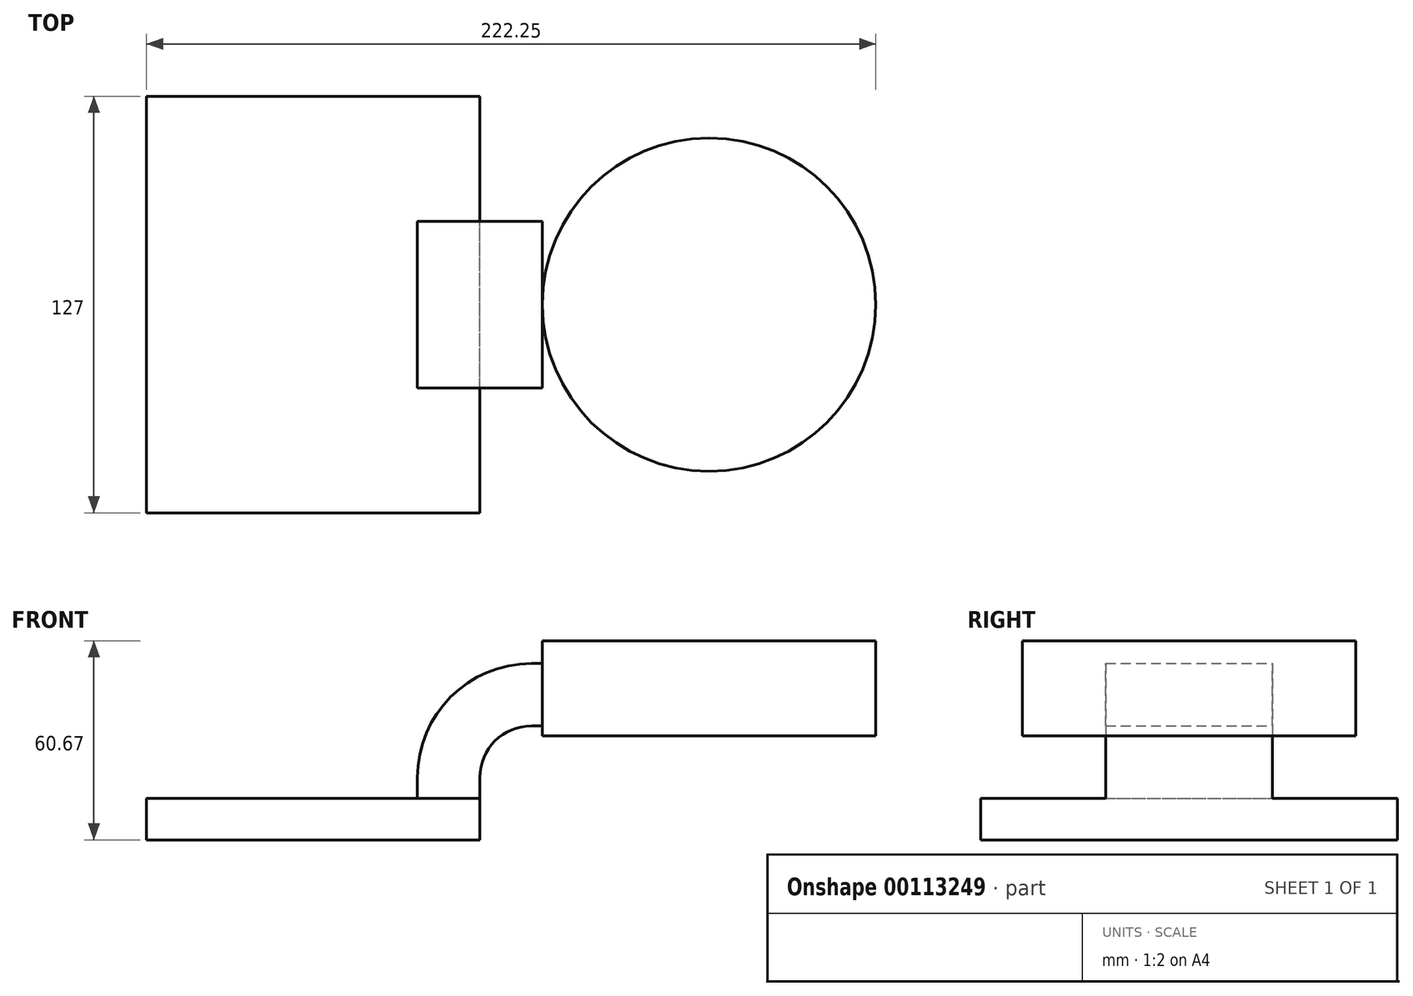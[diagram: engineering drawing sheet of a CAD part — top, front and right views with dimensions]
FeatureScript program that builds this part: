
annotation { "Feature Type Name" : "Feature", "Feature Type Description" : "" }
export const myFeature = defineFeature(function(context is Context, id is Id, definition is map)
    precondition{}
    {
        {
            var Q0;
            Q0=qCreatedBy(makeId("Front.planeOp"),FACE);
            var sketch = newSketch(context, id + "F0", { "sketchPlane" : qUnion([Q0])});
            skLineSegment(sketch, "E0.bottom", {"start": v(50.8, 6.35) * mm, "end": v(-50.8, 6.35) * mm});
            skLineSegment(sketch, "E0.top", {"start": v(50.8, -6.35) * mm, "end": v(-50.8, -6.35) * mm});
            skLineSegment(sketch, "E0.left", {"start": v(50.8, 6.35) * mm, "end": v(50.8, -6.35) * mm});
            skLineSegment(sketch, "E0.right", {"start": v(-50.8, 6.35) * mm, "end": v(-50.8, -6.35) * mm});
            skPoint(sketch, "E0.middle", {"position": v(0, 0) * mm});
            skLineSegment(sketch, "E1.bottom", {"start": v(69.85, 25.4) * mm, "end": v(120.65, 25.4) * mm});
            skLineSegment(sketch, "E1.top", {"start": v(69.85, 54.32) * mm, "end": v(120.65, 54.32) * mm});
            skLineSegment(sketch, "E1.left", {"start": v(69.85, 25.4) * mm, "end": v(69.85, 54.32) * mm});
            skLineSegment(sketch, "E1.right", {"start": v(120.65, 25.4) * mm, "end": v(120.65, 54.32) * mm});
            skPoint(sketch, "E1.middle", {"position": v(95.25, 39.86) * mm});
            skLineSegment(sketch, "E2", {"start": v(50.8, 6.35) * mm, "end": v(50.8, 12.7) * mm});
            skArc(sketch, "E3", {"start": v(50.8, 12.7) * mm, "mid": v(55.39, 23.78) * mm, "end": v(66.47, 28.37) * mm});
            skLineSegment(sketch, "E4", {"start": v(66.47, 28.37) * mm, "end": v(90.85, 28.37) * mm});
            skLineSegment(sketch, "E5.0", {"start": v(66.47, 47.42) * mm, "end": v(90.85, 47.42) * mm});
            skArc(sketch, "E5.1", {"start": v(31.75, 12.7) * mm, "mid": v(41.92, 37.25) * mm, "end": v(66.47, 47.42) * mm});
            skLineSegment(sketch, "E5.2", {"start": v(31.75, 12.7) * mm, "end": v(31.75, 35.55) * mm});
            skLineSegment(sketch, "E6", {"start": v(31.75, 12.7) * mm, "end": v(31.75, 6.35) * mm});
            skSolve(sketch);
        }
        {
            var Q0;
            Q0=makeQuery(id+"F0.imprint","IMPRINT",FACE,{"disambiguationData":[TD([[makeQuery(id+"F0.imprint","IMPRINT",EDGE,{"derivedFrom":sQuery(id+"F0.wireOp",EDGE,"E0.top")}),-1.0]])]});
            extrude(context, id + "F1", {"entities" : qUnion([Q0]), "endBound" : BoundingType.SYMMETRIC, "depth" : 127 * mm});
        }
        {
            var Q0;
            {var subQ2=sQuery(id+"F0.wireOp",EDGE,"E2");Q0=makeQuery(id+"F0.imprint","IMPRINT",FACE,{"disambiguationData":[TD([[makeQuery(id+"F0.imprint","IMPRINT",EDGE,{"derivedFrom":subQ2}),1.0]])]});}
            extrude(context, id + "F2", {"entities" : qUnion([Q0]), "operationType" : NewBodyOperationType.ADD, "endBound" : BoundingType.SYMMETRIC, "depth" : 50.8 * mm});
        }
        {
            var Q0;
            {var subQ3=sQuery(id+"F0.wireOp",EDGE,"E1.bottom");Q0=makeQuery(id+"F0.imprint","IMPRINT",FACE,{"disambiguationData":[TD([[makeQuery(id+"F0.imprint","IMPRINT",EDGE,{"derivedFrom":subQ3}),1.0]])]});}
            var Q1;
            Q1=sQuery(id+"F0.wireOp",EDGE,"E1.right");
            revolve(context, id + "F3", {"operationType" : NewBodyOperationType.ADD, "entities" : qUnion([Q0]), "axis" : qUnion([Q1]), "revolveType" : RevolveType.FULL});
        }
    });
